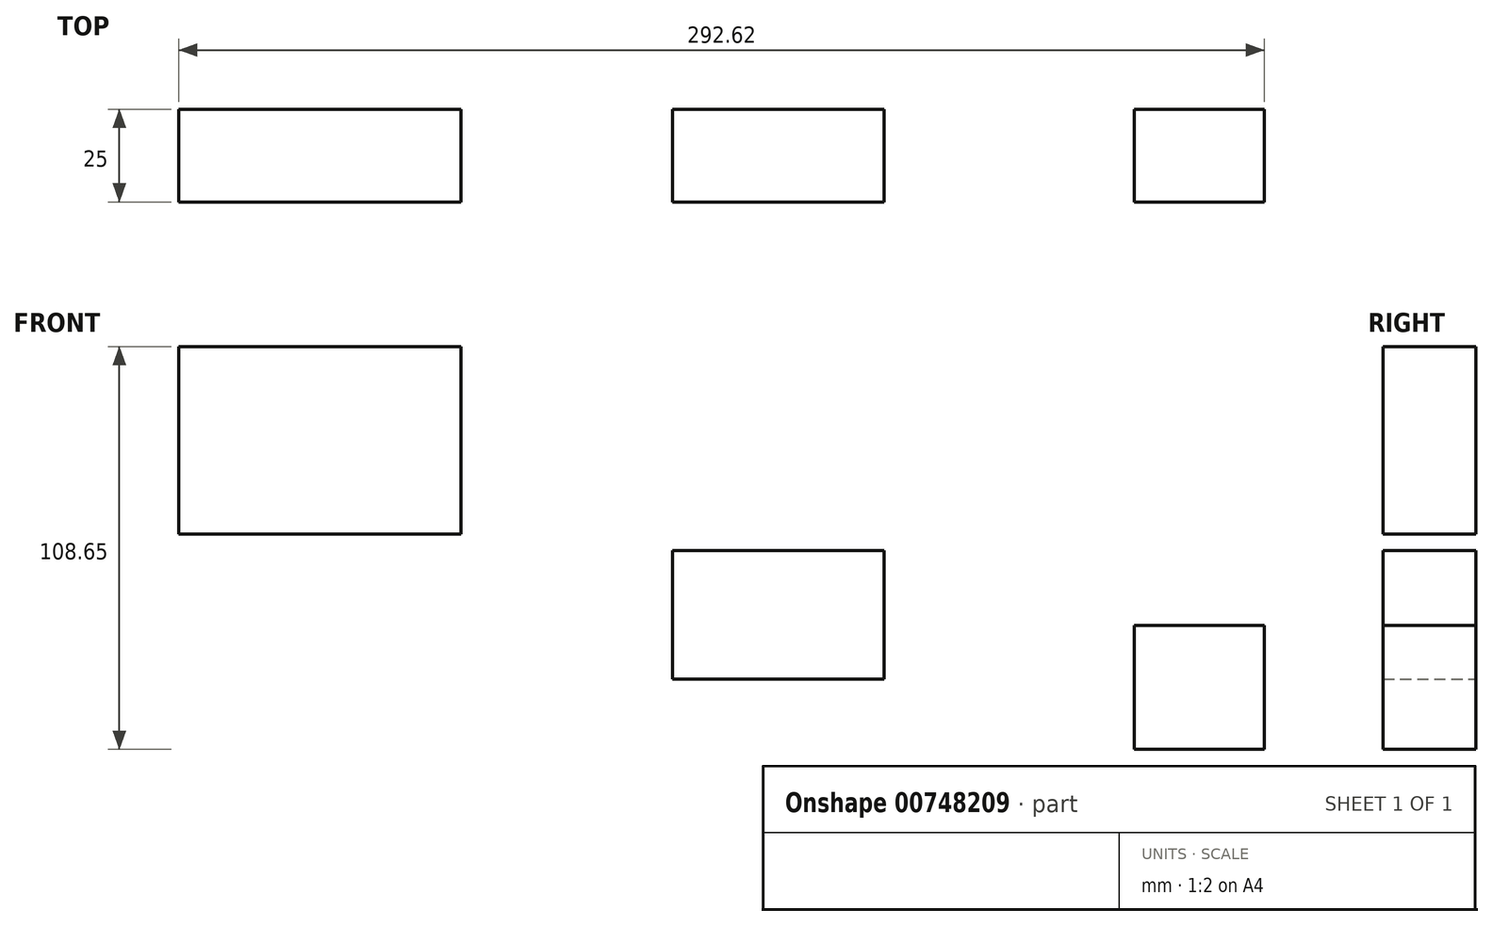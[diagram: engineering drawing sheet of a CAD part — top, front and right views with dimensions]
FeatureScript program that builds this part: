
annotation { "Feature Type Name" : "Feature", "Feature Type Description" : "" }
export const myFeature = defineFeature(function(context is Context, id is Id, definition is map)
    precondition{}
    {
        {
            var Q0;
            Q0=qCreatedBy(makeId("Front.planeOp"),FACE);
            var sketch = newSketch(context, id + "F0", { "sketchPlane" : qUnion([Q0])});
            skLineSegment(sketch, "E0.bottom", {"start": v(-159.15, 75.2) * mm, "end": v(-83.1, 75.2) * mm});
            skLineSegment(sketch, "E0.top", {"start": v(-159.15, 24.57) * mm, "end": v(-83.1, 24.57) * mm});
            skLineSegment(sketch, "E0.left", {"start": v(-159.15, 75.2) * mm, "end": v(-159.15, 24.57) * mm});
            skLineSegment(sketch, "E0.right", {"start": v(-83.1, 75.2) * mm, "end": v(-83.1, 24.57) * mm});
            skLineSegment(sketch, "E1.bottom", {"start": v(-26.05, 20.13) * mm, "end": v(31, 20.13) * mm});
            skLineSegment(sketch, "E1.top", {"start": v(-26.05, -14.45) * mm, "end": v(31, -14.45) * mm});
            skLineSegment(sketch, "E1.left", {"start": v(-26.05, 20.13) * mm, "end": v(-26.05, -14.45) * mm});
            skLineSegment(sketch, "E1.right", {"start": v(31, 20.13) * mm, "end": v(31, -14.45) * mm});
            skLineSegment(sketch, "E2.bottom", {"start": v(133.47, 0) * mm, "end": v(98.4, 0) * mm});
            skLineSegment(sketch, "E2.top", {"start": v(133.47, -33.46) * mm, "end": v(98.4, -33.46) * mm});
            skLineSegment(sketch, "E2.left", {"start": v(133.47, 0) * mm, "end": v(133.47, -33.46) * mm});
            skLineSegment(sketch, "E2.right", {"start": v(98.4, 0) * mm, "end": v(98.4, -33.46) * mm});
            skSolve(sketch);
        }
        {
            var Q0;
            Q0 = qSketchRegion(id + "F0", true);
            extrude(context, id + "F1", {"entities" : qUnion([Q0]), "depth" : 25 * mm, "offsetDistance" : 25 * mm});
        }
    });
